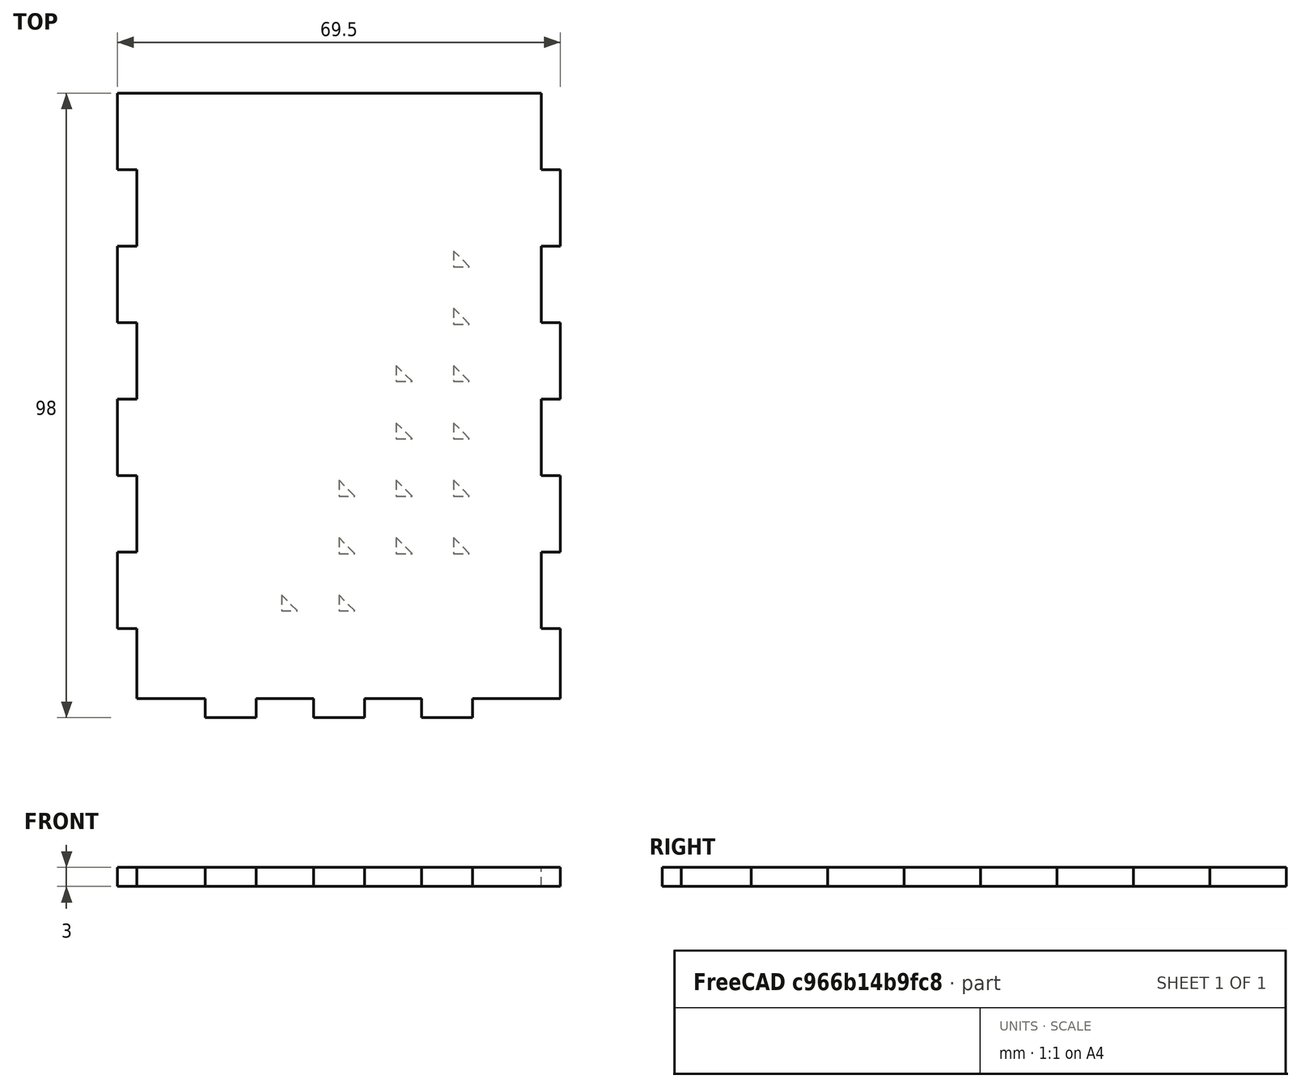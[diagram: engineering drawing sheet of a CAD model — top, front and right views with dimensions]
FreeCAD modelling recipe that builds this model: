
FCSTD DOCUMENT
Label: tea-light-side-circlesFCStd
objects: Sketcher::SketchObject×2, PartDesign::LinearPattern×2, PartDesign::Pad×1, PartDesign::Pocket×1, PartDesign::MultiTransform×1
note: 9 computed .brp shape members not serialized (recipe doc carries the construction recipe); baked Part::Feature solids carry a one-line shape summary decoded from their .brp

FEATURE [Sketcher::SketchObject] Sketch
  sketch-geometry (44):
    g0: LineSegment StartX=34.75 StartY=-29 StartZ=0 EndX=21 EndY=-29 EndZ=0
    g1: LineSegment StartX=21 StartY=-29 StartZ=0 EndX=21 EndY=-32 EndZ=0
    g2: LineSegment StartX=21 StartY=-32 StartZ=0 EndX=13 EndY=-32 EndZ=0
    g3: LineSegment StartX=13 StartY=-32 StartZ=0 EndX=13 EndY=-29 EndZ=0
    g4: LineSegment StartX=13 StartY=-29 StartZ=0 EndX=4 EndY=-29 EndZ=0
    g5: LineSegment StartX=4 StartY=-29 StartZ=0 EndX=4 EndY=-32 EndZ=0
    g6: LineSegment StartX=4 StartY=-32 StartZ=0 EndX=-4 EndY=-32 EndZ=0
    g7: LineSegment StartX=-4 StartY=-32 StartZ=0 EndX=-4 EndY=-29 EndZ=0
    g8: LineSegment StartX=-4 StartY=-29 StartZ=0 EndX=-13 EndY=-29 EndZ=0
    g9: LineSegment StartX=-13 StartY=-29 StartZ=0 EndX=-13 EndY=-32 EndZ=0
    g10: LineSegment StartX=-13 StartY=-32 StartZ=0 EndX=-21 EndY=-32 EndZ=0
    g11: LineSegment StartX=-21 StartY=-32 StartZ=0 EndX=-21 EndY=-29 EndZ=0
    g12: LineSegment StartX=-21 StartY=-29 StartZ=0 EndX=-31.75 EndY=-29 EndZ=0
    g13: LineSegment StartX=-31.75 StartY=-29 StartZ=0 EndX=-31.75 EndY=-18 EndZ=0
    g14: LineSegment StartX=-31.75 StartY=-18 StartZ=0 EndX=-34.75 EndY=-18 EndZ=0
    g15: LineSegment StartX=-34.75 StartY=-18 StartZ=0 EndX=-34.75 EndY=-6 EndZ=0
    g16: LineSegment StartX=-34.75 StartY=-6 StartZ=0 EndX=-31.75 EndY=-6 EndZ=0
    g17: LineSegment StartX=-31.75 StartY=-6 StartZ=0 EndX=-31.75 EndY=6 EndZ=0
    g18: LineSegment StartX=-31.75 StartY=6 StartZ=0 EndX=-34.75 EndY=6 EndZ=0
    g19: LineSegment StartX=-34.75 StartY=6 StartZ=0 EndX=-34.75 EndY=18 EndZ=0
    g20: LineSegment StartX=-34.75 StartY=18 StartZ=0 EndX=-31.75 EndY=18 EndZ=0
    g21: LineSegment StartX=-31.75 StartY=18 StartZ=0 EndX=-31.75 EndY=30 EndZ=0
    g22: LineSegment StartX=-31.75 StartY=30 StartZ=0 EndX=-34.75 EndY=30 EndZ=0
    g23: LineSegment StartX=-34.75 StartY=30 StartZ=0 EndX=-34.75 EndY=42 EndZ=0
    g24: LineSegment StartX=-34.75 StartY=42 StartZ=0 EndX=-31.75 EndY=42 EndZ=0
    g25: LineSegment StartX=-31.75 StartY=42 StartZ=0 EndX=-31.75 EndY=54 EndZ=0
    g26: LineSegment StartX=-31.75 StartY=54 StartZ=0 EndX=-34.75 EndY=54 EndZ=0
    g27: LineSegment StartX=-34.75 StartY=54 StartZ=0 EndX=-34.75 EndY=66 EndZ=0
    g28: LineSegment StartX=-34.75 StartY=66 StartZ=0 EndX=31.75 EndY=66 EndZ=0
    g29: LineSegment StartX=31.75 StartY=66 StartZ=0 EndX=31.75 EndY=54 EndZ=0
    g30: LineSegment StartX=31.75 StartY=54 StartZ=0 EndX=34.75 EndY=54 EndZ=0
    g31: LineSegment StartX=34.75 StartY=54 StartZ=0 EndX=34.75 EndY=42 EndZ=0
    g32: LineSegment StartX=34.75 StartY=42 StartZ=0 EndX=31.75 EndY=42 EndZ=0
    g33: LineSegment StartX=31.75 StartY=42 StartZ=0 EndX=31.75 EndY=30 EndZ=0
    g34: LineSegment StartX=31.75 StartY=30 StartZ=0 EndX=34.75 EndY=30 EndZ=0
    g35: LineSegment StartX=34.75 StartY=30 StartZ=0 EndX=34.75 EndY=18 EndZ=0
    g36: LineSegment StartX=34.75 StartY=18 StartZ=0 EndX=31.75 EndY=18 EndZ=0
    g37: LineSegment StartX=31.75 StartY=18 StartZ=0 EndX=31.75 EndY=6 EndZ=0
    g38: LineSegment StartX=31.75 StartY=6 StartZ=0 EndX=34.75 EndY=6 EndZ=0
    g39: LineSegment StartX=34.75 StartY=6 StartZ=0 EndX=34.75 EndY=-6 EndZ=0
    g40: LineSegment StartX=34.75 StartY=-6 StartZ=0 EndX=31.75 EndY=-6 EndZ=0
    g41: LineSegment StartX=31.75 StartY=-6 StartZ=0 EndX=31.75 EndY=-18 EndZ=0
    g42: LineSegment StartX=31.75 StartY=-18 StartZ=0 EndX=34.75 EndY=-18 EndZ=0
    g43: LineSegment StartX=34.75 StartY=-18 StartZ=0 EndX=34.75 EndY=-29 EndZ=0
  constraints (132):
    c: Horizontal(g0)
    c: Coincident(g0,g1)
    c: Vertical(g1)
    c: Coincident(g1,g2)
    c: Horizontal(g2)
    c: Coincident(g2,g3)
    c: Vertical(g3)
    c: Coincident(g3,g4)
    c: Horizontal(g4)
    c: Coincident(g4,g5)
    c: Vertical(g5)
    c: Coincident(g5,g6)
    c: Coincident(g6,g7)
    c: Vertical(g7)
    c: Coincident(g7,g8)
    c: Horizontal(g8)
    c: Coincident(g8,g9)
    c: Vertical(g9)
    c: Coincident(g9,g10)
    c: Horizontal(g10)
    c: Coincident(g10,g11)
    c: Vertical(g11)
    c: Coincident(g11,g12)
    c: Horizontal(g12)
    c: Coincident(g12,g13)
    c: Vertical(g13)
    c: Coincident(g13,g14)
    c: Coincident(g14,g15)
    c: Vertical(g15)
    c: Coincident(g15,g16)
    c: Horizontal(g16)
    c: Coincident(g16,g17)
    c: Vertical(g17)
    c: Coincident(g17,g18)
    c: Coincident(g18,g19)
    c: Vertical(g19)
    c: Coincident(g19,g20)
    c: Coincident(g20,g21)
    c: Coincident(g21,g22)
    c: Horizontal(g22)
    c: Coincident(g22,g23)
    c: Vertical(g23)
    c: Coincident(g23,g24)
    c: Horizontal(g24)
    c: Coincident(g24,g25)
    c: Vertical(g25)
    c: Coincident(g25,g26)
    c: Horizontal(g26)
    c: Coincident(g26,g27)
    c: Vertical(g27)
    c: Coincident(g27,g28)
    c: Horizontal(g28)
    c: Coincident(g28,g29)
    c: Vertical(g29)
    c: Coincident(g29,g30)
    c: Horizontal(g30)
    c: Coincident(g30,g31)
    c: Vertical(g31)
    c: Coincident(g31,g32)
    c: Coincident(g32,g33)
    c: Vertical(g33)
    c: Coincident(g33,g34)
    c: Coincident(g34,g35)
    c: Coincident(g35,g36)
    c: Coincident(g36,g37)
    c: Vertical(g37)
    c: Coincident(g37,g38)
    c: Horizontal(g38)
    c: Coincident(g38,g39)
    c: Coincident(g39,g40)
    c: Horizontal(g40)
    c: Coincident(g40,g41)
    c: Coincident(g41,g42)
    c: Horizontal(g42)
    c: Coincident(g42,g43)
    c: Coincident(g43,g0)
    c: Horizontal(g14)
    c: Horizontal(g18)
    c: Horizontal(g20)
    c: Horizontal(g36)
    c: Horizontal(g32)
    c: Horizontal(g34)
    c: Vertical(g21)
    c: Vertical(g41)
    c: Vertical(g43)
    c: Vertical(g35)
    c: Vertical(g39)
    c: Symmetric(g25,g29,g-2)
    c: DistanceY(g7,g27) = 95
    c: DistanceX(g25,g29) = 63.5
    c: Equal(g11,g9)
    c: Equal(g9,g7)
    c: Equal(g7,g5)
    c: Equal(g5,g3)
    c: Equal(g3,g1)
    c: Equal(g38,g36)
    c: Equal(g36,g34)
    c: Equal(g34,g32)
    c: Equal(g32,g30)
    c: Equal(g30,g40)
    c: Equal(g40,g42)
    c: Equal(g1,g42)
    c: Equal(g14,g16)
    c: Equal(g16,g18)
    c: Equal(g18,g20)
    c: Equal(g20,g22)
    c: Equal(g22,g24)
    c: Equal(g24,g26)
    c: DistanceY(g1) = -3
    c: Equal(g14,g11)
    c: Equal(g10,g6)
    c: Equal(g6,g2)
    c: Equal(g8,g4)
    c: Symmetric(g6,g5,g-2)
    c: DistanceX(g10) = -8
    c: DistanceX(g4) = -9
    c: Equal(g13,g43)
    c: Equal(g15,g41)
    c: Equal(g17,g39)
    c: Equal(g19,g37)
    c: Equal(g35,g21)
    c: Equal(g23,g33)
    c: Equal(g25,g31)
    c: Equal(g27,g29)
    c: Symmetric(g38,g39,g-1)
    c: Equal(g23,g19)
    c: Equal(g19,g15)
    c: Equal(g17,g21)
    c: Equal(g21,g25)
    c: DistanceY(g37) = -12
    c: DistanceY(g35) = -12
    c: DistanceY(g27) = 12
FEATURE [PartDesign::Pad] Pad
  Length = 3
  Length2 = 100
  Sketch = -> Sketch
  Type = 0
FEATURE [Sketcher::SketchObject] Sketch001
  ExternalGeometry = -> [Pad]
  Placement = pos=(0,0,3) rot=(0,0,1;0rad)
  Support = -> Pad [Face46]
  sketch-geometry (20):
    g0: Circle CenterX=-22.5 CenterY=-19.75 CenterZ=0 NormalX=0 NormalY=0 NormalZ=1 Radius=3.5
    g1: LineSegment StartX=-27 StartY=-15.25 StartZ=0 EndX=-24.5 EndY=-15.25 EndZ=0
    g2: LineSegment StartX=-24.5 StartY=-15.25 StartZ=0 EndX=-27 EndY=-17.75 EndZ=0
    g3: LineSegment StartX=-27 StartY=-17.75 StartZ=0 EndX=-27 EndY=-15.25 EndZ=0
    g4: LineSegment StartX=-20.5 StartY=-15.25 StartZ=0 EndX=-18 EndY=-15.25 EndZ=0
    g5: LineSegment StartX=-18 StartY=-15.25 StartZ=0 EndX=-18 EndY=-17.75 EndZ=0
    g6: LineSegment StartX=-18 StartY=-17.75 StartZ=0 EndX=-20.5 EndY=-15.25 EndZ=0
    g7: LineSegment [constr] StartX=-27 StartY=-15.25 StartZ=0 EndX=-22.5 EndY=-19.75 EndZ=0
    g8: LineSegment StartX=-27 StartY=-21.75 StartZ=0 EndX=-24.5 EndY=-24.25 EndZ=0
    g9: LineSegment StartX=-24.5 StartY=-24.25 StartZ=0 EndX=-27 EndY=-24.25 EndZ=0
    g10: LineSegment StartX=-27 StartY=-24.25 StartZ=0 EndX=-27 EndY=-21.75 EndZ=0
    g11: LineSegment [constr] StartX=-22.5 StartY=-19.75 StartZ=0 EndX=-18 EndY=-15.25 EndZ=0
    g12: LineSegment [constr] StartX=-22.5 StartY=-19.75 StartZ=0 EndX=-27 EndY=-24.25 EndZ=0
    g13: LineSegment StartX=-20.5 StartY=-24.25 StartZ=0 EndX=-18 EndY=-21.75 EndZ=0
    g14: LineSegment StartX=-18 StartY=-21.75 StartZ=0 EndX=-18 EndY=-24.25 EndZ=0
    g15: LineSegment StartX=-18 StartY=-24.25 StartZ=0 EndX=-20.5 EndY=-24.25 EndZ=0
    g16: LineSegment [constr] StartX=-22.5 StartY=-19.75 StartZ=0 EndX=-18 EndY=-24.25 EndZ=0
    g17: LineSegment [constr] StartX=-27 StartY=-17.75 StartZ=0 EndX=-27 EndY=-21.75 EndZ=0
    g18: LineSegment [constr] StartX=-24.5 StartY=-15.25 StartZ=0 EndX=-20.5 EndY=-15.25 EndZ=0
    g19: LineSegment [constr] StartX=-18 StartY=-21.75 StartZ=0 EndX=-18 EndY=-17.75 EndZ=0
  constraints (56):
    c: Coincident(g1,g2)
    c: Coincident(g2,g3)
    c: Coincident(g3,g1)
    c: Vertical(g3)
    c: Horizontal(g1)
    c: Horizontal(g4)
    c: Coincident(g4,g5)
    c: Vertical(g5)
    c: Coincident(g5,g6)
    c: Coincident(g6,g4)
    c: Equal(g3,g1)
    c: Equal(g1,g4)
    c: Equal(g4,g5)
    c: Coincident(g8,g9)
    c: Horizontal(g9)
    c: Coincident(g9,g10)
    c: Coincident(g10,g8)
    c: Vertical(g10)
    c: Coincident(g7,g1)
    c: Equal(g10,g3)
    c: Equal(g3,g9)
    c: Equal(g9,g5)
    c: Equal(g5,g4)
    c: Coincident(g11,g4)
    c: Coincident(g12,g9)
    c: Coincident(g13,g14)
    c: Vertical(g14)
    c: Coincident(g14,g15)
    c: Coincident(g15,g13)
    c: Horizontal(g15)
    c: Equal(g15,g14)
    c: Equal(g14,g5)
    c: Coincident(g17,g2)
    c: Coincident(g17,g8)
    c: Vertical(g17)
    c: Equal(g7,g12)
    c: Equal(g12,g16)
    c: Equal(g16,g11)
    c: Coincident(g16,g14)
    c: Coincident(g18,g1)
    c: Horizontal(g18)
    c: Coincident(g4,g18)
    c: Equal(g18,g17)
    c: Coincident(g19,g5)
    c: Coincident(g19,g13)
    c: Vertical(g19)
    c: Equal(g19,g18)
    c: Radius(g0) = 3.5
    c: DistanceX(g1,g4) = 9
    c: DistanceY(g5) = -2.5
    c: Coincident(g7,g0)
    c: Coincident(g12,g11)
    c: Coincident(g11,g0)
    c: Coincident(g16,g0)
    c: DistanceX(g-2,g4) = -18
    c: Distance(g9,g-4) = 4.75
FEATURE [PartDesign::Pocket] Pocket
  Length = 5
  Sketch = -> Sketch001
  Type = 0
FEATURE [PartDesign::LinearPattern] LinearPattern
  Direction = -> Sketch001 [H_Axis]
  Length = 45
  Occurrences = 6
FEATURE [PartDesign::LinearPattern] LinearPattern001
  Direction = -> Sketch001 [V_Axis]
  Length = 72
  Occurrences = 9
FEATURE [PartDesign::MultiTransform] MultiTransform
  Originals = -> [Pocket]
  Transformations = -> [LinearPattern,LinearPattern001]
